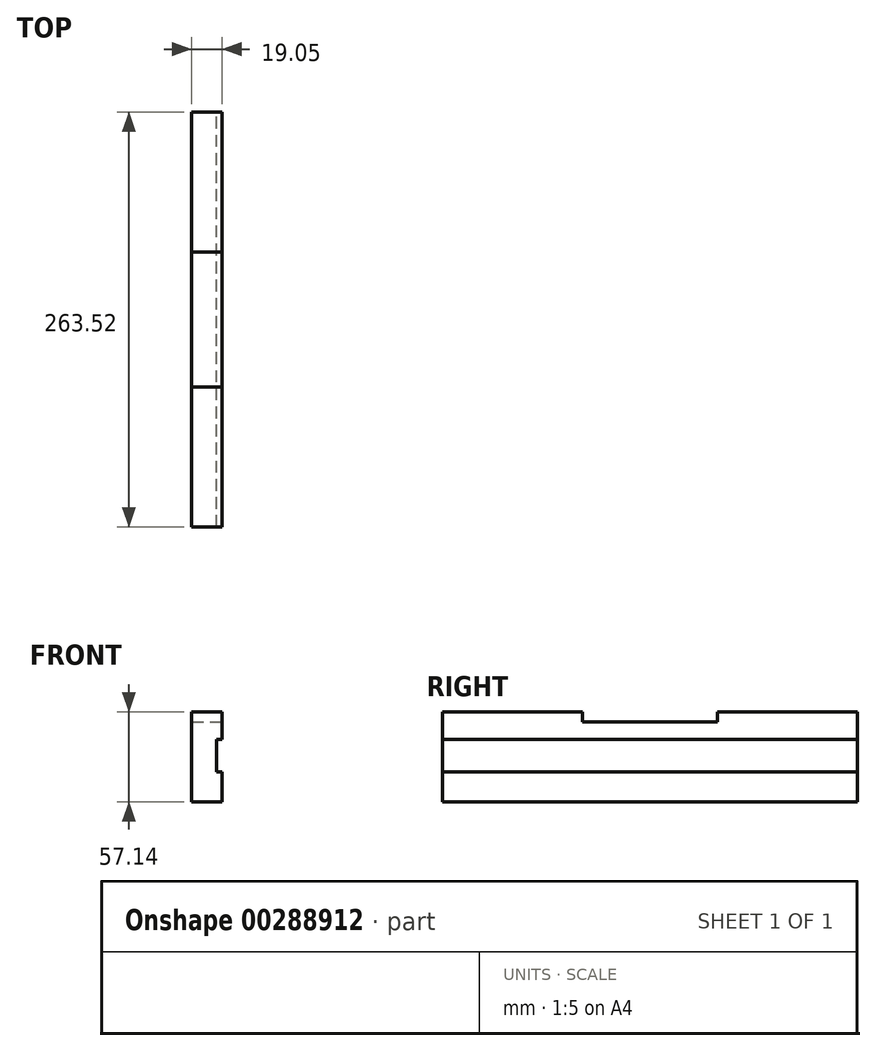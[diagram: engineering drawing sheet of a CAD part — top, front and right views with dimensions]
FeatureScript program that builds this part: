
annotation { "Feature Type Name" : "Feature", "Feature Type Description" : "" }
export const myFeature = defineFeature(function(context is Context, id is Id, definition is map)
    precondition{}
    {
        {
            var Q0;
            Q0=qCreatedBy(makeId("Right.planeOp"),FACE);
            var sketch = newSketch(context, id + "F0", { "sketchPlane" : qUnion([Q0])});
            skLineSegment(sketch, "E0.bottom", {"start": v(-131.76, -28.57) * mm, "end": v(131.76, -28.57) * mm});
            skLineSegment(sketch, "E0.top", {"start": v(-131.76, 28.57) * mm, "end": v(131.76, 28.57) * mm});
            skLineSegment(sketch, "E0.left", {"start": v(-131.76, -28.57) * mm, "end": v(-131.76, 28.57) * mm});
            skLineSegment(sketch, "E0.right", {"start": v(131.76, -28.57) * mm, "end": v(131.76, 28.57) * mm});
            skPoint(sketch, "E0.middle", {"position": v(0, 0) * mm});
            skSolve(sketch);
        }
        {
            var Q0;
            Q0 = qSketchRegion(id + "F0", true);
            extrude(context, id + "F1", {"entities" : qUnion([Q0]), "depth" : 19.05 * mm});
        }
        {
            var Q0;
            Q0=makeQuery(id+"F1.opExtrude","CAP_FACE",FACE,{"disambiguationData":[OSD([sQuery(id+"F0.wireOp",EDGE,"E0.bottom"),sQuery(id+"F0.wireOp",EDGE,"E0.top"),sQuery(id+"F0.wireOp",EDGE,"E0.left"),sQuery(id+"F0.wireOp",EDGE,"E0.right")])],"isStart":false});
            var sketch = newSketch(context, id + "F2", { "sketchPlane" : qUnion([Q0])});
            skPoint(sketch, "E1.middle", {"position": v(0, 0) * mm});
            skLineSegment(sketch, "E2", {"start": v(-131.76, 28.57) * mm, "end": v(-131.76, -28.57) * mm, "construction": true});
            skLineSegment(sketch, "E3", {"start": v(131.76, 28.57) * mm, "end": v(131.76, -28.57) * mm, "construction": true});
            skLineSegment(sketch, "E4", {"start": v(-131.76, -9.52) * mm, "end": v(131.76, -9.52) * mm, "construction": true});
            skLineSegment(sketch, "E5.bottom", {"start": v(-131.76, -9.52) * mm, "end": v(131.76, -9.52) * mm});
            skLineSegment(sketch, "E5.top", {"start": v(-131.76, 11.18) * mm, "end": v(131.76, 11.18) * mm});
            skLineSegment(sketch, "E5.left", {"start": v(-131.76, -9.52) * mm, "end": v(-131.76, 11.18) * mm});
            skLineSegment(sketch, "E5.right", {"start": v(131.76, -9.52) * mm, "end": v(131.76, 11.18) * mm});
            skSolve(sketch);
        }
        {
            var Q0;
            Q0 = qSketchRegion(id + "F2", true);
            extrude(context, id + "F3", {"entities" : qUnion([Q0]), "operationType" : NewBodyOperationType.REMOVE, "oppositeDirection" : true, "depth" : 3.17 * mm});
        }
        {
            var Q0;
            {var subQ0=sQuery(id+"F0.wireOp",EDGE,"E0.top");var subQ1=sQuery(id+"F0.wireOp",EDGE,"E0.left");var subQ2=sQuery(id+"F0.wireOp",EDGE,"E0.right");Q0=makeQuery(id+"F3.boolean.opBoolean","SPLIT",FACE,{"disambiguationData":[TD([makeQuery(id+"F1.opExtrude","SWEPT_FACE",FACE,{"disambiguationData":[OSD([subQ0])]})])],"derivedFrom":makeQuery(id+"F1.opExtrude","CAP_FACE",FACE,{"disambiguationData":[OSD([sQuery(id+"F0.wireOp",EDGE,"E0.bottom"),subQ0,subQ1,subQ2])],"isStart":false})});}
            var sketch = newSketch(context, id + "F4", { "sketchPlane" : qUnion([Q0])});
            skLineSegment(sketch, "E6.bottom", {"start": v(-42.86, 28.57) * mm, "end": v(42.86, 28.57) * mm});
            skLineSegment(sketch, "E6.top", {"start": v(-42.86, 22.22) * mm, "end": v(42.86, 22.22) * mm});
            skLineSegment(sketch, "E6.left", {"start": v(-42.86, 28.57) * mm, "end": v(-42.86, 22.22) * mm});
            skLineSegment(sketch, "E6.right", {"start": v(42.86, 28.57) * mm, "end": v(42.86, 22.22) * mm});
            skSolve(sketch);
        }
        {
            var Q0;
            Q0 = qSketchRegion(id + "F4", true);
            extrude(context, id + "F5", {"entities" : qUnion([Q0]), "operationType" : NewBodyOperationType.REMOVE, "endBound" : BoundingType.UP_TO_NEXT, "oppositeDirection" : true, "depth" : 25.4 * mm});
        }
    });
